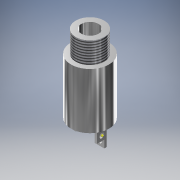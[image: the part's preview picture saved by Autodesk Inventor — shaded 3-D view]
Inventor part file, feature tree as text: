
AUTODESK INVENTOR PART (.ipt)
format: ipt  version: 2016 (Build 200138000, 138)  size: 168,448 bytes
history: native  units: mm
features: sketch x10, extrude x7, other x3, thread x1
ambient origin geometry x8: Origin, YZ Plane, XZ Plane, XY Plane, X Axis, Y Axis, Z Axis, Center Point
bodies: Solid1 (feature_tree)
feature tree (21):
  extrude  "Extrusion1"  Depth=11.7mm TaperAngle=0.0deg
  extrude  "Extrusion2"  Depth=4.5mm TaperAngle=0.0deg
  thread  "Thread1"  [1 undecoded]
  extrude  "Extrusion3"  Depth=15.0mm TaperAngle=0.0deg
  extrude  "Extrusion4"  Depth=0.5mm
  extrude  "Extrusion5"  Depth=1.0mm
  extrude  "Extrusion6"  Depth=2.0mm
  extrude  "Extrusion7"  Depth=2.0mm
  sketch  "Sketch8"  dims[d20=1.0mm]
  other  "ring"
  sketch  "Sketch9"  dims[d21=6.1mm d22=0.0mm]
  other  "sleve"
  sketch  "Sketch10"  dims[d23=1.0mm d24=1.0mm d25=6.1mm d26=0.0mm d27=1.0mm d28=1.0mm d29=6.1mm d30=0.0mm]
  other  "tip"
  sketch  "Sketch1"  dims[d0=8.0mm d1=11.7mm d2=0.0mm]
  sketch  "Sketch2"  dims[d3=6.0mm d4=4.5mm d5=0.0mm d6=10.0mm d7=0.0mm]
  sketch  "Sketch3"  dims[d8=3.6mm d9=15.0mm d10=0.0mm]
  sketch  "Sketch4"  dims[d11=2.0mm d12=0.5mm]
  sketch  "Sketch5"  dims[d13=2.0mm d14=1.0mm]
  sketch  "Sketch6"  dims[d15=3.0mm d16=0.0mm d17=2.0mm]
  sketch  "Sketch7"  dims[d18=0.5mm d19=2.0mm]
note: 1 required parameter value undecoded (feature->parameter linkage not recoverable at this tier; creation-order binding heuristic only, values carry confidence <= 0.55)
